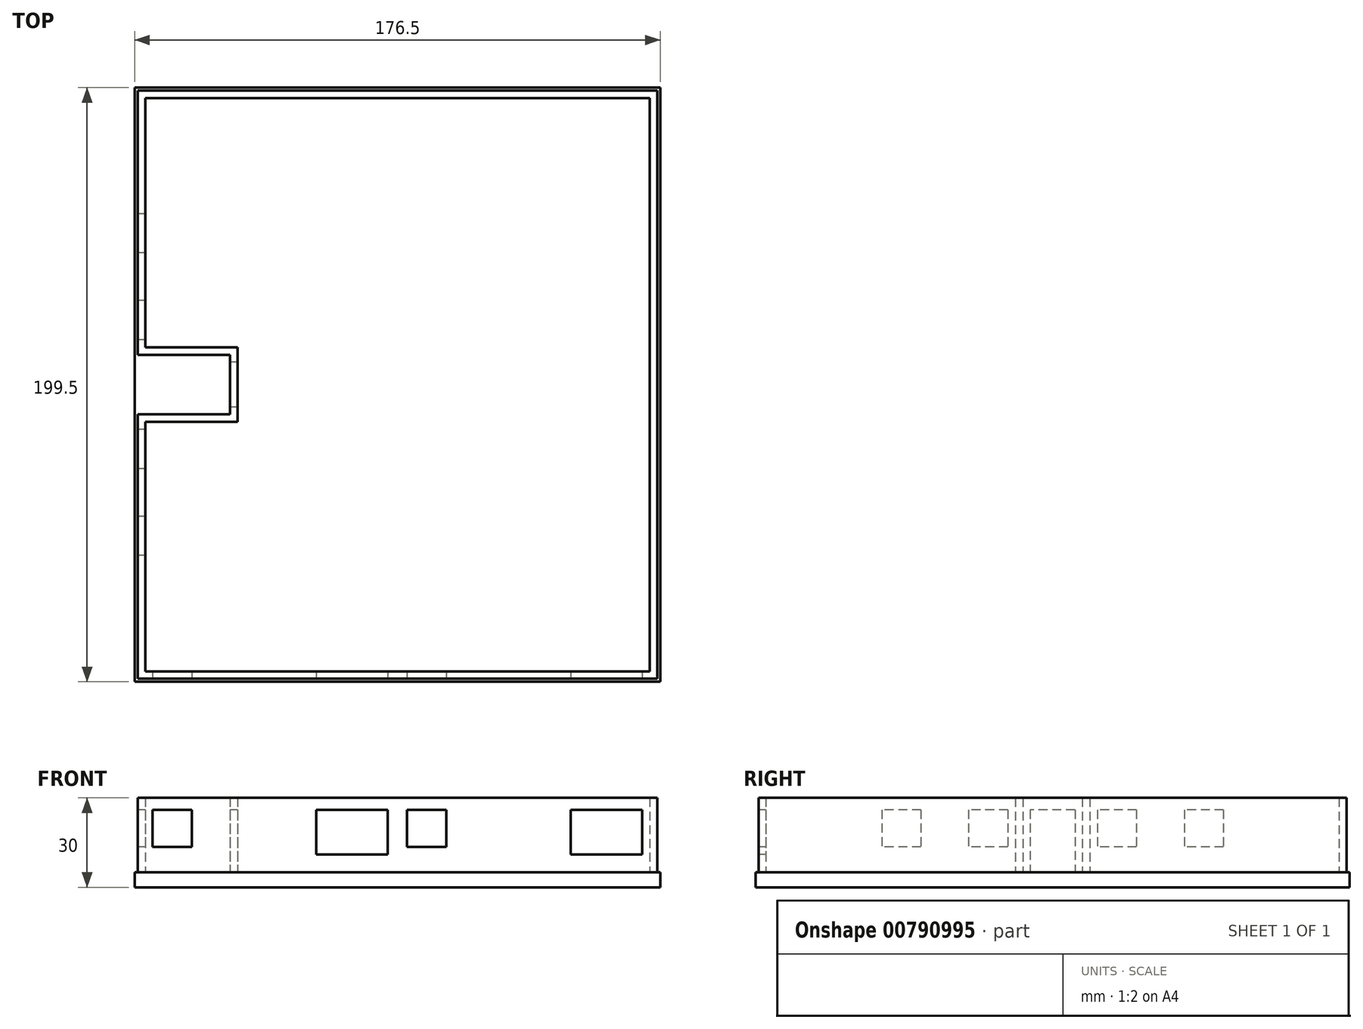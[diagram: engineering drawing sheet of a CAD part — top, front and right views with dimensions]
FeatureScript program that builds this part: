
annotation { "Feature Type Name" : "Feature", "Feature Type Description" : "" }
export const myFeature = defineFeature(function(context is Context, id is Id, definition is map)
    precondition{}
    {
        {
            var Q0;
            Q0=qCreatedBy(makeId("Top.planeOp"),FACE);
            var sketch = newSketch(context, id + "F0", { "sketchPlane" : qUnion([Q0])});
            skLineSegment(sketch, "E0.bottom", {"start": v(-145.38, 121) * mm, "end": v(31.12, 121) * mm});
            skLineSegment(sketch, "E0.top", {"start": v(-145.38, -78.5) * mm, "end": v(31.12, -78.5) * mm});
            skLineSegment(sketch, "E0.left", {"start": v(-145.38, 121) * mm, "end": v(-145.38, -78.5) * mm});
            skLineSegment(sketch, "E0.right", {"start": v(31.12, 121) * mm, "end": v(31.12, -78.5) * mm});
            skSolve(sketch);
        }
        {
            var Q0;
            Q0=makeQuery(id+"F0.imprint","IMPRINT",FACE,{"disambiguationData":[TD([[makeQuery(id+"F0.imprint","IMPRINT",EDGE,{"derivedFrom":sQuery(id+"F0.wireOp",EDGE,"E0.bottom")}),-1.0]])]});
            extrude(context, id + "F1", {"entities" : qUnion([Q0]), "depth" : 5 * mm, "offsetDistance" : 25 * mm});
        }
        {
            var Q0;
            Q0=makeQuery(id+"F1.opExtrude","CAP_FACE",FACE,{"disambiguationData":[OSD([sQuery(id+"F0.wireOp",EDGE,"E0.bottom"),sQuery(id+"F0.wireOp",EDGE,"E0.top"),sQuery(id+"F0.wireOp",EDGE,"E0.left"),sQuery(id+"F0.wireOp",EDGE,"E0.right")])],"isStart":false});
            var sketch = newSketch(context, id + "F2", { "sketchPlane" : qUnion([Q0])});
            skLineSegment(sketch, "E1.0", {"start": v(-144.38, 120) * mm, "end": v(-144.38, -77.5) * mm});
            skLineSegment(sketch, "E1.1", {"start": v(30.12, 120) * mm, "end": v(-144.38, 120) * mm});
            skLineSegment(sketch, "E1.2", {"start": v(30.12, -77.5) * mm, "end": v(30.12, 120) * mm});
            skLineSegment(sketch, "E1.3", {"start": v(-144.38, -77.5) * mm, "end": v(30.12, -77.5) * mm});
            skLineSegment(sketch, "E2.bottom", {"start": v(-144.38, 31.3) * mm, "end": v(-113.38, 31.3) * mm});
            skLineSegment(sketch, "E2.top", {"start": v(-144.38, 11.3) * mm, "end": v(-113.38, 11.3) * mm});
            skLineSegment(sketch, "E2.left", {"start": v(-144.38, 31.3) * mm, "end": v(-144.38, 11.3) * mm});
            skLineSegment(sketch, "E2.right", {"start": v(-113.38, 31.3) * mm, "end": v(-113.38, 11.3) * mm});
            skLineSegment(sketch, "E3.0", {"start": v(27.62, 117.5) * mm, "end": v(-144.38, 117.5) * mm});
            skLineSegment(sketch, "E3.1", {"start": v(27.62, -75) * mm, "end": v(27.62, 117.5) * mm});
            skLineSegment(sketch, "E3.2", {"start": v(-144.38, -75) * mm, "end": v(27.62, -75) * mm});
            skLineSegment(sketch, "E4.0", {"start": v(-144.38, 8.8) * mm, "end": v(-110.88, 8.8) * mm});
            skLineSegment(sketch, "E4.1", {"start": v(-110.88, 33.8) * mm, "end": v(-110.88, 8.8) * mm});
            skLineSegment(sketch, "E4.2", {"start": v(-144.38, 33.8) * mm, "end": v(-110.88, 33.8) * mm});
            skLineSegment(sketch, "E5", {"start": v(-141.88, 117.5) * mm, "end": v(-141.88, 33.8) * mm});
            skLineSegment(sketch, "E6", {"start": v(-141.88, 8.8) * mm, "end": v(-141.88, -75) * mm});
            skSolve(sketch);
        }
        {
            var Q0;
            {var subQ0=sQuery(id+"F2.wireOp",EDGE,"aAtNQeyO-9I3L-dpeZ-mZV7-1GNY1PWUIx9j");Q0=makeQuery(id+"F2.imprint","IMPRINT",FACE,{"disambiguationData":[TD([[makeQuery(id+"F2.imprint","IMPRINT",EDGE,{"derivedFrom":subQ0}),-1.0]])]});}
            var Q1;
            {var subQ0=sQuery(id+"F2.wireOp",EDGE,"Zs0VbnZ2-orGb-vHb7-zxmX-7qJMPkJ84dtN");Q1=makeQuery(id+"F2.imprint","IMPRINT",FACE,{"disambiguationData":[TD([[makeQuery(id+"F2.imprint","IMPRINT",EDGE,{"derivedFrom":subQ0}),1.0]])]});}
            var Q2;
            {var subQ6=sQuery(id+"F2.wireOp",EDGE,"E2.top");Q2=makeQuery(id+"F2.imprint","IMPRINT",FACE,{"disambiguationData":[TD([[makeQuery(id+"F2.imprint","IMPRINT",EDGE,{"derivedFrom":subQ6}),-1.0]])]});}
            var Q3;
            {var subQ0=sQuery(id+"F2.wireOp",EDGE,"E2.right");Q3=makeQuery(id+"F2.imprint","IMPRINT",FACE,{"disambiguationData":[TD([[makeQuery(id+"F2.imprint","IMPRINT",EDGE,{"derivedFrom":subQ0}),1.0]])]});}
            var Q4;
            {var subQ4=sQuery(id+"F2.wireOp",EDGE,"E2.bottom");Q4=makeQuery(id+"F2.imprint","IMPRINT",FACE,{"disambiguationData":[TD([[makeQuery(id+"F2.imprint","IMPRINT",EDGE,{"derivedFrom":subQ4}),1.0]])]});}
            var Q5;
            {var subQ5=sQuery(id+"F2.wireOp",EDGE,"E5");Q5=makeQuery(id+"F2.imprint","IMPRINT",FACE,{"disambiguationData":[TD([[makeQuery(id+"F2.imprint","IMPRINT",EDGE,{"derivedFrom":subQ5}),-1.0]])]});}
            var Q6;
            {var subQ7=sQuery(id+"F2.wireOp",EDGE,"E1.1");Q6=makeQuery(id+"F2.imprint","IMPRINT",FACE,{"disambiguationData":[TD([[makeQuery(id+"F2.imprint","IMPRINT",EDGE,{"derivedFrom":subQ7}),1.0]])]});}
            var Q7;
            {var subQ5=sQuery(id+"F2.wireOp",EDGE,"E6");Q7=makeQuery(id+"F2.imprint","IMPRINT",FACE,{"disambiguationData":[TD([[makeQuery(id+"F2.imprint","IMPRINT",EDGE,{"derivedFrom":subQ5}),-1.0]])]});}
            extrude(context, id + "F3", {"entities" : qUnion([Q0, Q1, Q2, Q3, Q4, Q5, Q6, Q7]), "operationType" : NewBodyOperationType.ADD, "depth" : 25 * mm, "offsetDistance" : 25 * mm});
        }
        {
            var Q0;
            Q0=makeQuery(id+"F3.opExtrude","SWEPT_FACE",FACE,{"disambiguationData":[OSD([sQuery(id+"F2.wireOp",EDGE,"E2.right")])]});
            var sketch = newSketch(context, id + "F4", { "sketchPlane" : qUnion([Q0])});
            skLineSegment(sketch, "E7.bottom", {"start": v(-28.8, 26) * mm, "end": v(-13.8, 26) * mm});
            skLineSegment(sketch, "E7.top", {"start": v(-28.8, 5) * mm, "end": v(-13.8, 5) * mm});
            skLineSegment(sketch, "E7.left", {"start": v(-28.8, 26) * mm, "end": v(-28.8, 5) * mm});
            skLineSegment(sketch, "E7.right", {"start": v(-13.8, 26) * mm, "end": v(-13.8, 5) * mm});
            skSolve(sketch);
        }
        {
            var Q0;
            Q0=makeQuery(id+"F4.imprint","IMPRINT",FACE,{"disambiguationData":[TD([[makeQuery(id+"F4.imprint","IMPRINT",EDGE,{"derivedFrom":sQuery(id+"F4.wireOp",EDGE,"E7.bottom")}),-1.0]])]});
            extrude(context, id + "F5", {"entities" : qUnion([Q0]), "operationType" : NewBodyOperationType.REMOVE, "endBound" : BoundingType.UP_TO_NEXT, "oppositeDirection" : true, "depth" : 25 * mm, "offsetDistance" : 25 * mm});
        }
        {
            var Q0;
            {var subQ0=sQuery(id+"F2.wireOp",EDGE,"E1.0");var subQ1=makeQuery(id+"F2.imprint","INTERSECT",VERTEX,{"derivedFrom":[subQ0,sQuery(id+"F2.wireOp",EDGE,"E4.2")]});var subQ2=makeQuery(id+"F2.imprint","INTERSECT",VERTEX,{"derivedFrom":[subQ0,sQuery(id+"F2.wireOp",EDGE,"E3.0")]});Q0=makeQuery(id+"F3.opExtrude","SWEPT_FACE",FACE,{"disambiguationData":[OSD([subQ0]),TDD([makeQuery(id+"F2.imprint","IMPRINT",EDGE,{"disambiguationData":[TD([[makeQuery(id+"F2.imprint","INTERSECT",VERTEX,{"derivedFrom":[subQ0,sQuery(id+"F2.wireOp",EDGE,"E1.1")]}),-1.0]])],"derivedFrom":subQ0}),makeQuery(id+"F2.imprint","IMPRINT",EDGE,{"disambiguationData":[TD([[subQ2,-1.0]])],"derivedFrom":subQ0}),makeQuery(id+"F2.imprint","IMPRINT",EDGE,{"disambiguationData":[TD([[subQ1,-1.0]])],"derivedFrom":subQ0})])]});}
            var sketch = newSketch(context, id + "F6", { "sketchPlane" : qUnion([Q0])});
            skLineSegment(sketch, "E8.bottom", {"start": v(-78.7, 26) * mm, "end": v(-65.5, 26) * mm});
            skLineSegment(sketch, "E8.top", {"start": v(-78.7, 13.6) * mm, "end": v(-65.5, 13.6) * mm});
            skLineSegment(sketch, "E8.left", {"start": v(-78.7, 26) * mm, "end": v(-78.7, 13.6) * mm});
            skLineSegment(sketch, "E8.right", {"start": v(-65.5, 26) * mm, "end": v(-65.5, 13.6) * mm});
            skLineSegment(sketch, "E9.bottom", {"start": v(-49.5, 26) * mm, "end": v(-36.3, 26) * mm});
            skLineSegment(sketch, "E9.top", {"start": v(-49.5, 13.6) * mm, "end": v(-36.3, 13.6) * mm});
            skLineSegment(sketch, "E9.left", {"start": v(-49.5, 26) * mm, "end": v(-49.5, 13.6) * mm});
            skLineSegment(sketch, "E9.right", {"start": v(-36.3, 26) * mm, "end": v(-36.3, 13.6) * mm});
            skLineSegment(sketch, "E10.bottom", {"start": v(-6.3, 26) * mm, "end": v(6.9, 26) * mm});
            skLineSegment(sketch, "E10.top", {"start": v(-6.3, 13.6) * mm, "end": v(6.9, 13.6) * mm});
            skLineSegment(sketch, "E10.left", {"start": v(-6.3, 26) * mm, "end": v(-6.3, 13.6) * mm});
            skLineSegment(sketch, "E10.right", {"start": v(6.9, 26) * mm, "end": v(6.9, 13.6) * mm});
            skLineSegment(sketch, "E11.bottom", {"start": v(22.9, 26) * mm, "end": v(36.1, 26) * mm});
            skLineSegment(sketch, "E11.top", {"start": v(22.9, 13.6) * mm, "end": v(36.1, 13.6) * mm});
            skLineSegment(sketch, "E11.left", {"start": v(22.9, 26) * mm, "end": v(22.9, 13.6) * mm});
            skLineSegment(sketch, "E11.right", {"start": v(36.1, 26) * mm, "end": v(36.1, 13.6) * mm});
            skSolve(sketch);
        }
        {
            var Q0;
            Q0=makeQuery(id+"F6.imprint","IMPRINT",FACE,{"disambiguationData":[TD([[makeQuery(id+"F6.imprint","IMPRINT",EDGE,{"derivedFrom":sQuery(id+"F6.wireOp",EDGE,"E8.bottom")}),-1.0]])]});
            var Q1;
            Q1=makeQuery(id+"F6.imprint","IMPRINT",FACE,{"disambiguationData":[TD([[makeQuery(id+"F6.imprint","IMPRINT",EDGE,{"derivedFrom":sQuery(id+"F6.wireOp",EDGE,"E9.bottom")}),-1.0]])]});
            var Q2;
            Q2=makeQuery(id+"F6.imprint","IMPRINT",FACE,{"disambiguationData":[TD([[makeQuery(id+"F6.imprint","IMPRINT",EDGE,{"derivedFrom":sQuery(id+"F6.wireOp",EDGE,"E10.bottom")}),-1.0]])]});
            var Q3;
            Q3=makeQuery(id+"F6.imprint","IMPRINT",FACE,{"disambiguationData":[TD([[makeQuery(id+"F6.imprint","IMPRINT",EDGE,{"derivedFrom":sQuery(id+"F6.wireOp",EDGE,"E11.bottom")}),-1.0]])]});
            extrude(context, id + "F7", {"entities" : qUnion([Q0, Q1, Q2, Q3]), "operationType" : NewBodyOperationType.REMOVE, "endBound" : BoundingType.UP_TO_NEXT, "oppositeDirection" : true, "depth" : 25 * mm, "offsetDistance" : 25 * mm});
        }
        {
            var Q0;
            Q0=makeQuery(id+"F3.opExtrude","SWEPT_FACE",FACE,{"disambiguationData":[OSD([sQuery(id+"F2.wireOp",EDGE,"E1.3")])]});
            var sketch = newSketch(context, id + "F8", { "sketchPlane" : qUnion([Q0])});
            skLineSegment(sketch, "E12.bottom", {"start": v(-139.38, 26) * mm, "end": v(-126.18, 26) * mm});
            skLineSegment(sketch, "E12.top", {"start": v(-139.38, 13.6) * mm, "end": v(-126.18, 13.6) * mm});
            skLineSegment(sketch, "E12.left", {"start": v(-139.38, 26) * mm, "end": v(-139.38, 13.6) * mm});
            skLineSegment(sketch, "E12.right", {"start": v(-126.18, 26) * mm, "end": v(-126.18, 13.6) * mm});
            skLineSegment(sketch, "E13.bottom", {"start": v(-84.38, 26) * mm, "end": v(-60.38, 26) * mm});
            skLineSegment(sketch, "E13.top", {"start": v(-84.38, 11) * mm, "end": v(-60.38, 11) * mm});
            skLineSegment(sketch, "E13.left", {"start": v(-84.38, 26) * mm, "end": v(-84.38, 11) * mm});
            skLineSegment(sketch, "E13.right", {"start": v(-60.38, 26) * mm, "end": v(-60.38, 11) * mm});
            skLineSegment(sketch, "E14.bottom", {"start": v(-53.88, 26) * mm, "end": v(-40.68, 26) * mm});
            skLineSegment(sketch, "E14.top", {"start": v(-53.88, 13.6) * mm, "end": v(-40.68, 13.6) * mm});
            skLineSegment(sketch, "E14.left", {"start": v(-53.88, 26) * mm, "end": v(-53.88, 13.6) * mm});
            skLineSegment(sketch, "E14.right", {"start": v(-40.68, 26) * mm, "end": v(-40.68, 13.6) * mm});
            skLineSegment(sketch, "E15.bottom", {"start": v(1.12, 26) * mm, "end": v(25.12, 26) * mm});
            skLineSegment(sketch, "E15.top", {"start": v(1.12, 11) * mm, "end": v(25.12, 11) * mm});
            skLineSegment(sketch, "E15.left", {"start": v(1.12, 26) * mm, "end": v(1.12, 11) * mm});
            skLineSegment(sketch, "E15.right", {"start": v(25.12, 26) * mm, "end": v(25.12, 11) * mm});
            skSolve(sketch);
        }
        {
            var Q0;
            Q0 = qSketchRegion(id + "F8", true);
            extrude(context, id + "F9", {"entities" : qUnion([Q0]), "operationType" : NewBodyOperationType.REMOVE, "endBound" : BoundingType.UP_TO_NEXT, "oppositeDirection" : true, "depth" : 25 * mm, "offsetDistance" : 25 * mm});
        }
    });
